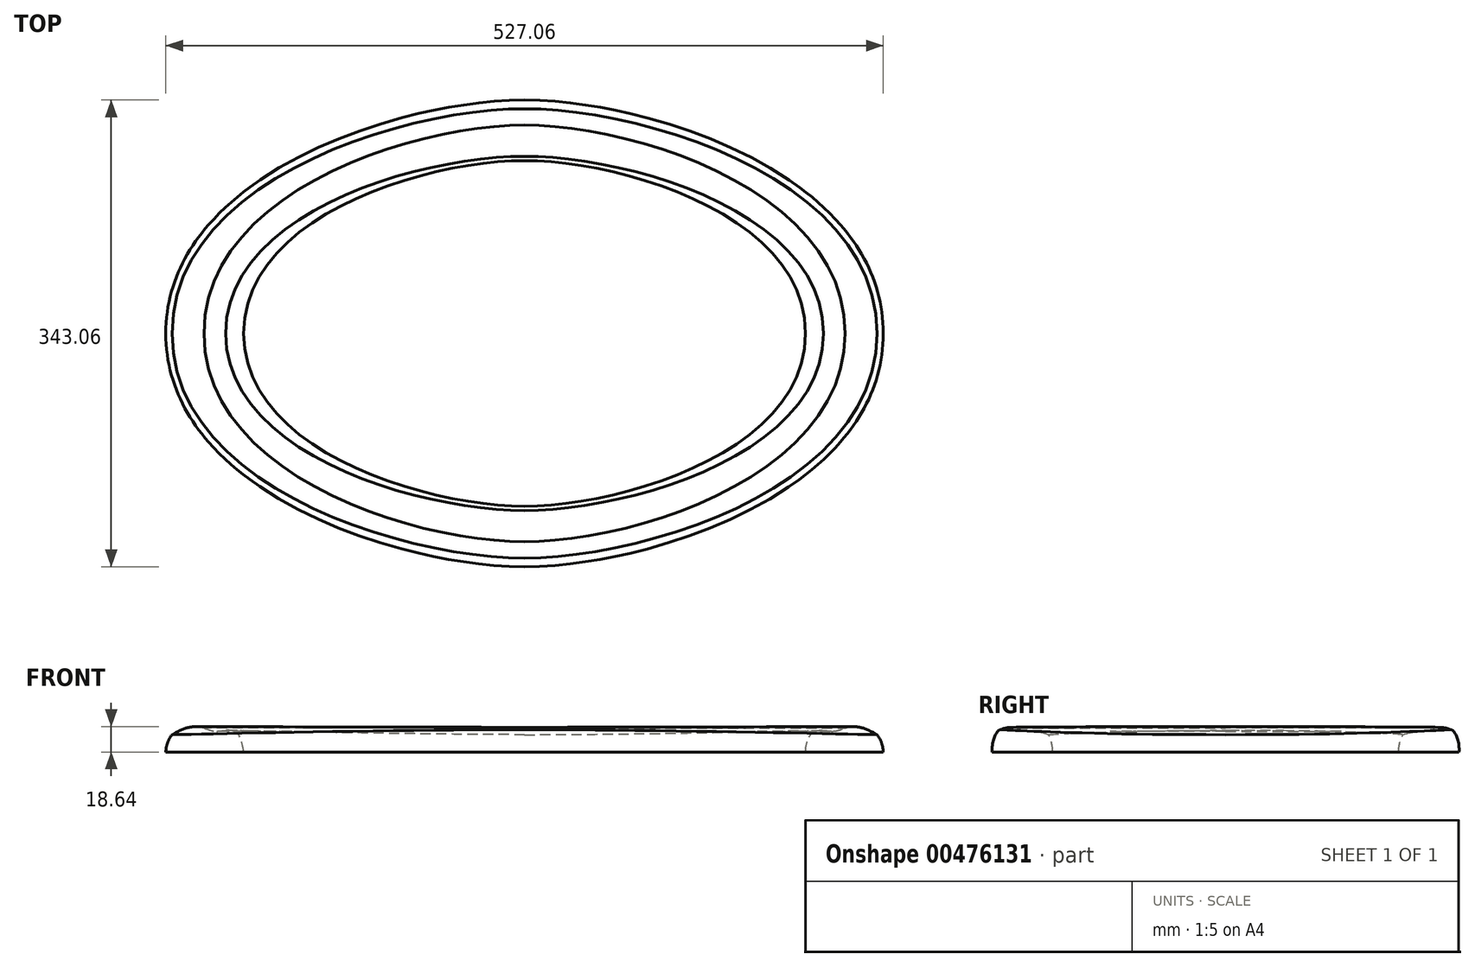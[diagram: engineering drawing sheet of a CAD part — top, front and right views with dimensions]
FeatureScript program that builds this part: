
annotation { "Feature Type Name" : "Feature", "Feature Type Description" : "" }
export const myFeature = defineFeature(function(context is Context, id is Id, definition is map)
    precondition{}
    {
        {
            var Q0;
            Q0=qCreatedBy(makeId("Right.planeOp"),FACE);
            var sketch = newSketch(context, id + "F0", { "sketchPlane" : qUnion([Q0])});
            skLineSegment(sketch, "E0", {"start": v(-127, 0) * mm, "end": v(-171.45, 0) * mm});
            skArc(sketch, "E1", {"start": v(-153.16, 17.78) * mm, "mid": v(-159.22, 17.98) * mm, "end": v(-165.1, 16.52) * mm});
            skArc(sketch, "E2", {"start": v(-127, 0) * mm, "mid": v(-127.86, 6.53) * mm, "end": v(-130.18, 12.7) * mm});
            skFitSpline(sketch, "E3", {"points": [v(-130.18, 12.7) * mm, v(-153.16, 17.78) * mm], "startDerivative": vector(-37.81, 13.1) * mm, "endDerivative": vector(-26.3, 14.45) * mm});
            skFitSpline(sketch, "E4", {"points": [v(-171.45, 0) * mm, v(-166.92, 15.69) * mm, v(-165.1, 16.52) * mm], "startDerivative": vector(-2.5, 29.76) * mm, "endDerivative": vector(3.72, 0.98) * mm});
            skPoint(sketch, "E5", {"position": v(-145.14, 15.19) * mm});
            skSolve(sketch);
        }
        {
            var Q0;
            Q0=qCreatedBy(makeId("Front.planeOp"),FACE);
            var sketch = newSketch(context, id + "F1", { "sketchPlane" : qUnion([Q0])});
            skLineSegment(sketch, "E6", {"start": v(206.38, 0) * mm, "end": v(263.52, 0) * mm});
            skFitSpline(sketch, "E7", {"points": [v(206.38, 0) * mm, v(226.7, 15.24) * mm, v(258.95, 12.7) * mm], "startDerivative": vector(12.01, 135.94) * mm, "endDerivative": vector(109.06, -64.99) * mm});
            skFitSpline(sketch, "E8", {"points": [v(263.53, 0) * mm, v(258.95, 12.7) * mm], "startDerivative": vector(-1.1, 16.32) * mm, "endDerivative": vector(-8.43, 11.6) * mm});
            skPoint(sketch, "E9", {"position": v(240.2, 18.57) * mm});
            skSolve(sketch);
        }
        {
            var Q0;
            Q0 = qSketchRegion(id + "F0", true);
            var Q1;
            Q1 = qSketchRegion(id + "F1", true);
            loft(context, id + "F2", {"startCondition" : LoftEndDerivativeType.NORMAL_TO_PROFILE, "startMagnitude" : 1, "endCondition" : LoftEndDerivativeType.NORMAL_TO_PROFILE, "endMagnitude" : 1.9, "sheetProfilesArray" : [{ "sheetProfileEntities" : qUnion([Q0]) }, { "sheetProfileEntities" : qUnion([Q1]) }]});
        }
        {
            var Q0;
            {var subQ5=sQuery(id+"F0.wireOp",EDGE,"E0");Q0=makeQuery(id+"F2.opLoft","SWEPT_BODY",BODY,{"disambiguationData":[OSD([makeQuery(id+"F0.imprint","IMPRINT",FACE,{"disambiguationData":[TD([[makeQuery(id+"F0.imprint","IMPRINT",EDGE,{"derivedFrom":subQ5}),-1.0]])]}),makeQuery(id+"F1.imprint","IMPRINT",FACE,{"disambiguationData":[TD([[makeQuery(id+"F1.imprint","IMPRINT",EDGE,{"derivedFrom":sQuery(id+"F1.wireOp",EDGE,"E6")}),1.0]])]})])]});}
            var Q1;
            Q1=qCreatedBy(makeId("Front.planeOp"),FACE);
            mirror(context, id + "F3", {"operationType" : NewBodyOperationType.ADD, "entities" : qUnion([Q0]), "mirrorPlane" : qUnion([Q1])});
        }
        {
            var Q0;
            {var subQ5=sQuery(id+"F0.wireOp",EDGE,"E0");Q0=makeQuery(id+"F2.opLoft","SWEPT_BODY",BODY,{"disambiguationData":[OSD([makeQuery(id+"F0.imprint","IMPRINT",FACE,{"disambiguationData":[TD([[makeQuery(id+"F0.imprint","IMPRINT",EDGE,{"derivedFrom":subQ5}),-1.0]])]}),makeQuery(id+"F1.imprint","IMPRINT",FACE,{"disambiguationData":[TD([[makeQuery(id+"F1.imprint","IMPRINT",EDGE,{"derivedFrom":sQuery(id+"F1.wireOp",EDGE,"E6")}),1.0]])]})])]});}
            var Q1;
            Q1=qCreatedBy(makeId("Right.planeOp"),FACE);
            mirror(context, id + "F4", {"operationType" : NewBodyOperationType.ADD, "entities" : qUnion([Q0]), "mirrorPlane" : qUnion([Q1])});
        }
    });
